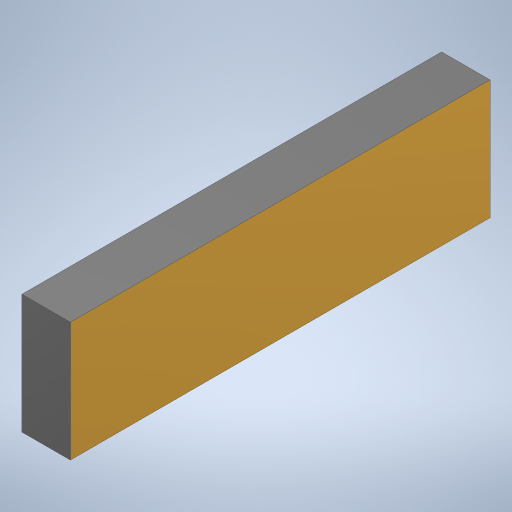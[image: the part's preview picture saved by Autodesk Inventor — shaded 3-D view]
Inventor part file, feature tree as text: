
AUTODESK INVENTOR PART (.ipt)
format: ipt  version: 2023 (Build 270158000, 158)  size: 196,608 bytes
history: native  units: mm
features: extrude x1, sketch x1
ambient origin geometry x8: Origin, YZ Plane, XZ Plane, XY Plane, X Axis, Y Axis, Z Axis, Center Point
bodies: 实体1 (feature_tree)
feature tree (2):
  extrude  "拉伸1"  Depth=2600.0mm
  sketch  "草图1"  dims[d0=740.0mm d1=2600.0mm d2=300.0mm d3=0.0mm]
